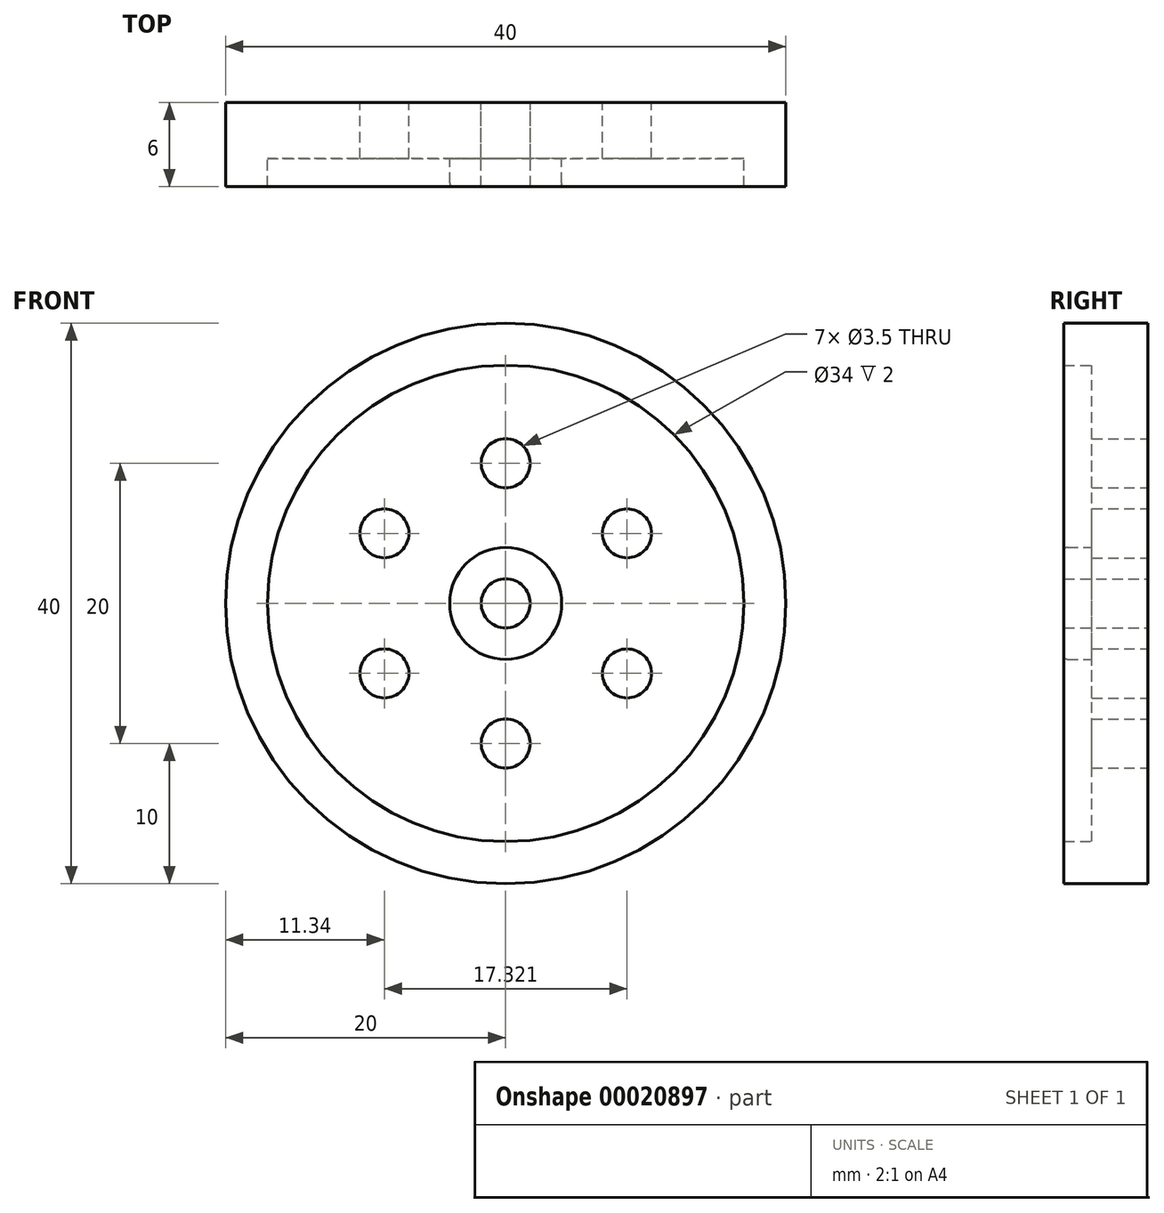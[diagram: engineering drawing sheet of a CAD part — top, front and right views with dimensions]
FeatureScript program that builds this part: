
annotation { "Feature Type Name" : "Feature", "Feature Type Description" : "" }
export const myFeature = defineFeature(function(context is Context, id is Id, definition is map)
    precondition{}
    {
        {
            var Q0;
            Q0=qCreatedBy(makeId("Front.planeOp"),FACE);
            var sketch = newSketch(context, id + "F0", { "sketchPlane" : qUnion([Q0])});
            skCircle(sketch, "E0", {"center": v(0, 0) * mm, "radius": 20 * mm});
            skCircle(sketch, "E1", {"center": v(0, 0) * mm, "radius": 1.75 * mm});
            skCircle(sketch, "E2.cCircle", {"center": v(0, 0) * mm, "radius": 20 * mm, "construction": true});
            skLineSegment(sketch, "E2.0", {"start": v(0, 20) * mm, "end": v(17.32, 10) * mm});
            skLineSegment(sketch, "E2.1", {"start": v(17.32, 10) * mm, "end": v(17.32, -10) * mm});
            skLineSegment(sketch, "E2.2", {"start": v(17.32, -10) * mm, "end": v(0, -20) * mm});
            skLineSegment(sketch, "E2.3", {"start": v(0, -20) * mm, "end": v(-17.32, -10) * mm});
            skLineSegment(sketch, "E2.4", {"start": v(-17.32, -10) * mm, "end": v(-17.32, 10) * mm});
            skLineSegment(sketch, "E2.5", {"start": v(-17.32, 10) * mm, "end": v(0, 20) * mm});
            skCircle(sketch, "E3", {"center": v(0, 0) * mm, "radius": 4 * mm});
            skLineSegment(sketch, "E4", {"start": v(0, 20) * mm, "end": v(0, 0) * mm});
            skLineSegment(sketch, "E5", {"start": v(0, 0) * mm, "end": v(-17.32, 10) * mm});
            skLineSegment(sketch, "E6", {"start": v(0, 0) * mm, "end": v(-17.32, -10) * mm});
            skLineSegment(sketch, "E7", {"start": v(0, 0) * mm, "end": v(0, -20) * mm});
            skLineSegment(sketch, "E8", {"start": v(0, 0) * mm, "end": v(17.32, -10) * mm});
            skLineSegment(sketch, "E9", {"start": v(0, 0) * mm, "end": v(17.32, 10) * mm});
            skCircle(sketch, "E10", {"center": v(0, 10) * mm, "radius": 1.75 * mm});
            skCircle(sketch, "E11", {"center": v(8.66, 5) * mm, "radius": 1.75 * mm});
            skCircle(sketch, "E12", {"center": v(0, -10) * mm, "radius": 1.75 * mm});
            skCircle(sketch, "E13", {"center": v(8.66, -5) * mm, "radius": 1.75 * mm});
            skCircle(sketch, "E14", {"center": v(-8.66, -5) * mm, "radius": 1.75 * mm});
            skCircle(sketch, "E15", {"center": v(-8.66, 5) * mm, "radius": 1.75 * mm});
            skCircle(sketch, "E16", {"center": v(0, 0) * mm, "radius": 17 * mm});
            skSolve(sketch);
        }
        {
            var Q0;
            {var subQ3=sQuery(id+"F0.wireOp",EDGE,"E4");var subQ11=sQuery(id+"F0.wireOp",EDGE,"E3");var subQ12=makeQuery(id+"F0.imprint","INTERSECT",VERTEX,{"derivedFrom":[subQ11,subQ3]});Q0=makeQuery(id+"F0.imprint","IMPRINT",FACE,{"disambiguationData":[TD([[makeQuery(id+"F0.imprint","IMPRINT",EDGE,{"disambiguationData":[TD([[subQ12,-1.0]])],"derivedFrom":subQ11}),-1.0]])]});}
            var Q1;
            {var subQ3=sQuery(id+"F0.wireOp",EDGE,"E5");var subQ11=sQuery(id+"F0.wireOp",EDGE,"E3");var subQ13=makeQuery(id+"F0.imprint","INTERSECT",VERTEX,{"derivedFrom":[subQ11,subQ3]});Q1=makeQuery(id+"F0.imprint","IMPRINT",FACE,{"disambiguationData":[TD([[makeQuery(id+"F0.imprint","IMPRINT",EDGE,{"disambiguationData":[TD([[subQ13,-1.0]])],"derivedFrom":subQ11}),-1.0]])]});}
            var Q2;
            {var subQ3=sQuery(id+"F0.wireOp",EDGE,"E6");var subQ11=sQuery(id+"F0.wireOp",EDGE,"E3");var subQ13=makeQuery(id+"F0.imprint","INTERSECT",VERTEX,{"derivedFrom":[subQ11,subQ3]});Q2=makeQuery(id+"F0.imprint","IMPRINT",FACE,{"disambiguationData":[TD([[makeQuery(id+"F0.imprint","IMPRINT",EDGE,{"disambiguationData":[TD([[subQ13,-1.0]])],"derivedFrom":subQ11}),-1.0]])]});}
            var Q3;
            {var subQ3=sQuery(id+"F0.wireOp",EDGE,"E7");var subQ11=sQuery(id+"F0.wireOp",EDGE,"E3");var subQ13=makeQuery(id+"F0.imprint","INTERSECT",VERTEX,{"derivedFrom":[subQ11,subQ3]});Q3=makeQuery(id+"F0.imprint","IMPRINT",FACE,{"disambiguationData":[TD([[makeQuery(id+"F0.imprint","IMPRINT",EDGE,{"disambiguationData":[TD([[subQ13,-1.0]])],"derivedFrom":subQ11}),-1.0]])]});}
            var Q4;
            {var subQ1=sQuery(id+"F0.wireOp",EDGE,"E9");var subQ11=sQuery(id+"F0.wireOp",EDGE,"E3");var subQ12=makeQuery(id+"F0.imprint","INTERSECT",VERTEX,{"derivedFrom":[subQ11,subQ1]});Q4=makeQuery(id+"F0.imprint","IMPRINT",FACE,{"disambiguationData":[TD([[makeQuery(id+"F0.imprint","IMPRINT",EDGE,{"disambiguationData":[TD([[subQ12,1.0]])],"derivedFrom":subQ11}),-1.0]])]});}
            var Q5;
            {var subQ6=sQuery(id+"F0.wireOp",EDGE,"E4");var subQ11=sQuery(id+"F0.wireOp",EDGE,"E3");var subQ13=makeQuery(id+"F0.imprint","INTERSECT",VERTEX,{"derivedFrom":[subQ11,subQ6]});Q5=makeQuery(id+"F0.imprint","IMPRINT",FACE,{"disambiguationData":[TD([[makeQuery(id+"F0.imprint","IMPRINT",EDGE,{"disambiguationData":[TD([[subQ13,1.0]])],"derivedFrom":subQ11}),-1.0]])]});}
            extrude(context, id + "F1", {"entities" : qUnion([Q0, Q1, Q2, Q3, Q4, Q5]), "depth" : 4 * mm});
        }
        {
            var Q0;
            {var subQ0=sQuery(id+"F0.wireOp",EDGE,"E2.5");Q0=makeQuery(id+"F0.imprint","IMPRINT",FACE,{"disambiguationData":[TD([[makeQuery(id+"F0.imprint","IMPRINT",EDGE,{"derivedFrom":subQ0}),1.0]])]});}
            var Q1;
            {var subQ6=sQuery(id+"F0.wireOp",EDGE,"E2.5");Q1=makeQuery(id+"F0.imprint","IMPRINT",FACE,{"disambiguationData":[TD([[makeQuery(id+"F0.imprint","IMPRINT",EDGE,{"derivedFrom":subQ6}),-1.0]])]});}
            var Q2;
            {var subQ6=sQuery(id+"F0.wireOp",EDGE,"E2.4");Q2=makeQuery(id+"F0.imprint","IMPRINT",FACE,{"disambiguationData":[TD([[makeQuery(id+"F0.imprint","IMPRINT",EDGE,{"derivedFrom":subQ6}),-1.0]])]});}
            var Q3;
            {var subQ0=sQuery(id+"F0.wireOp",EDGE,"E2.4");Q3=makeQuery(id+"F0.imprint","IMPRINT",FACE,{"disambiguationData":[TD([[makeQuery(id+"F0.imprint","IMPRINT",EDGE,{"derivedFrom":subQ0}),1.0]])]});}
            var Q4;
            {var subQ6=sQuery(id+"F0.wireOp",EDGE,"E2.3");Q4=makeQuery(id+"F0.imprint","IMPRINT",FACE,{"disambiguationData":[TD([[makeQuery(id+"F0.imprint","IMPRINT",EDGE,{"derivedFrom":subQ6}),-1.0]])]});}
            var Q5;
            {var subQ0=sQuery(id+"F0.wireOp",EDGE,"E2.3");Q5=makeQuery(id+"F0.imprint","IMPRINT",FACE,{"disambiguationData":[TD([[makeQuery(id+"F0.imprint","IMPRINT",EDGE,{"derivedFrom":subQ0}),1.0]])]});}
            var Q6;
            {var subQ6=sQuery(id+"F0.wireOp",EDGE,"E2.2");Q6=makeQuery(id+"F0.imprint","IMPRINT",FACE,{"disambiguationData":[TD([[makeQuery(id+"F0.imprint","IMPRINT",EDGE,{"derivedFrom":subQ6}),-1.0]])]});}
            var Q7;
            {var subQ0=sQuery(id+"F0.wireOp",EDGE,"E2.2");Q7=makeQuery(id+"F0.imprint","IMPRINT",FACE,{"disambiguationData":[TD([[makeQuery(id+"F0.imprint","IMPRINT",EDGE,{"derivedFrom":subQ0}),1.0]])]});}
            var Q8;
            {var subQ6=sQuery(id+"F0.wireOp",EDGE,"E2.1");Q8=makeQuery(id+"F0.imprint","IMPRINT",FACE,{"disambiguationData":[TD([[makeQuery(id+"F0.imprint","IMPRINT",EDGE,{"derivedFrom":subQ6}),-1.0]])]});}
            var Q9;
            {var subQ0=sQuery(id+"F0.wireOp",EDGE,"E2.1");Q9=makeQuery(id+"F0.imprint","IMPRINT",FACE,{"disambiguationData":[TD([[makeQuery(id+"F0.imprint","IMPRINT",EDGE,{"derivedFrom":subQ0}),1.0]])]});}
            var Q10;
            {var subQ6=sQuery(id+"F0.wireOp",EDGE,"E2.0");Q10=makeQuery(id+"F0.imprint","IMPRINT",FACE,{"disambiguationData":[TD([[makeQuery(id+"F0.imprint","IMPRINT",EDGE,{"derivedFrom":subQ6}),-1.0]])]});}
            var Q11;
            {var subQ0=sQuery(id+"F0.wireOp",EDGE,"E2.0");Q11=makeQuery(id+"F0.imprint","IMPRINT",FACE,{"disambiguationData":[TD([[makeQuery(id+"F0.imprint","IMPRINT",EDGE,{"derivedFrom":subQ0}),1.0]])]});}
            extrude(context, id + "F2", {"entities" : qUnion([Q0, Q1, Q2, Q3, Q4, Q5, Q6, Q7, Q8, Q9, Q10, Q11]), "operationType" : NewBodyOperationType.ADD, "depth" : 6 * mm});
        }
        {
            var Q0;
            {var subQ3=sQuery(id+"F0.wireOp",EDGE,"E1");var subQ5=sQuery(id+"F0.wireOp",EDGE,"E5");var subQ7=makeQuery(id+"F0.imprint","INTERSECT",VERTEX,{"derivedFrom":[subQ3,subQ5]});Q0=makeQuery(id+"F0.imprint","IMPRINT",FACE,{"disambiguationData":[TD([[makeQuery(id+"F0.imprint","IMPRINT",EDGE,{"disambiguationData":[TD([[subQ7,-1.0]])],"derivedFrom":subQ3}),-1.0]])]});}
            var Q1;
            {var subQ3=sQuery(id+"F0.wireOp",EDGE,"E1");var subQ5=sQuery(id+"F0.wireOp",EDGE,"E6");var subQ7=makeQuery(id+"F0.imprint","INTERSECT",VERTEX,{"derivedFrom":[subQ3,subQ5]});Q1=makeQuery(id+"F0.imprint","IMPRINT",FACE,{"disambiguationData":[TD([[makeQuery(id+"F0.imprint","IMPRINT",EDGE,{"disambiguationData":[TD([[subQ7,-1.0]])],"derivedFrom":subQ3}),-1.0]])]});}
            var Q2;
            {var subQ3=sQuery(id+"F0.wireOp",EDGE,"E1");var subQ5=sQuery(id+"F0.wireOp",EDGE,"E7");var subQ7=makeQuery(id+"F0.imprint","INTERSECT",VERTEX,{"derivedFrom":[subQ3,subQ5]});Q2=makeQuery(id+"F0.imprint","IMPRINT",FACE,{"disambiguationData":[TD([[makeQuery(id+"F0.imprint","IMPRINT",EDGE,{"disambiguationData":[TD([[subQ7,-1.0]])],"derivedFrom":subQ3}),-1.0]])]});}
            var Q3;
            {var subQ0=sQuery(id+"F0.wireOp",EDGE,"E9");var subQ3=sQuery(id+"F0.wireOp",EDGE,"E1");var subQ4=makeQuery(id+"F0.imprint","INTERSECT",VERTEX,{"derivedFrom":[subQ3,subQ0]});Q3=makeQuery(id+"F0.imprint","IMPRINT",FACE,{"disambiguationData":[TD([[makeQuery(id+"F0.imprint","IMPRINT",EDGE,{"disambiguationData":[TD([[subQ4,1.0]])],"derivedFrom":subQ3}),-1.0]])]});}
            var Q4;
            {var subQ3=sQuery(id+"F0.wireOp",EDGE,"E1");var subQ5=sQuery(id+"F0.wireOp",EDGE,"E4");var subQ7=makeQuery(id+"F0.imprint","INTERSECT",VERTEX,{"derivedFrom":[subQ3,subQ5]});Q4=makeQuery(id+"F0.imprint","IMPRINT",FACE,{"disambiguationData":[TD([[makeQuery(id+"F0.imprint","IMPRINT",EDGE,{"disambiguationData":[TD([[subQ7,1.0]])],"derivedFrom":subQ3}),-1.0]])]});}
            var Q5;
            {var subQ3=sQuery(id+"F0.wireOp",EDGE,"E1");var subQ5=sQuery(id+"F0.wireOp",EDGE,"E4");var subQ7=makeQuery(id+"F0.imprint","INTERSECT",VERTEX,{"derivedFrom":[subQ3,subQ5]});Q5=makeQuery(id+"F0.imprint","IMPRINT",FACE,{"disambiguationData":[TD([[makeQuery(id+"F0.imprint","IMPRINT",EDGE,{"disambiguationData":[TD([[subQ7,-1.0]])],"derivedFrom":subQ3}),-1.0]])]});}
            extrude(context, id + "F3", {"entities" : qUnion([Q0, Q1, Q2, Q3, Q4, Q5]), "operationType" : NewBodyOperationType.ADD, "depth" : 6 * mm});
        }
        {
            var Q0;
            Q0=makeQuery(id+"F3.opExtrude","CAP_EDGE",EDGE,{"disambiguationData":[OSD([sQuery(id+"F0.wireOp",EDGE,"E3")])],"isStart":false});
            fillet(context, id + "F4", {"entities" : qUnion([Q0]), "radius" : .25 * mm, "tangentPropagation" : true, "allowEdgeOverflow" : false});
        }
    });
